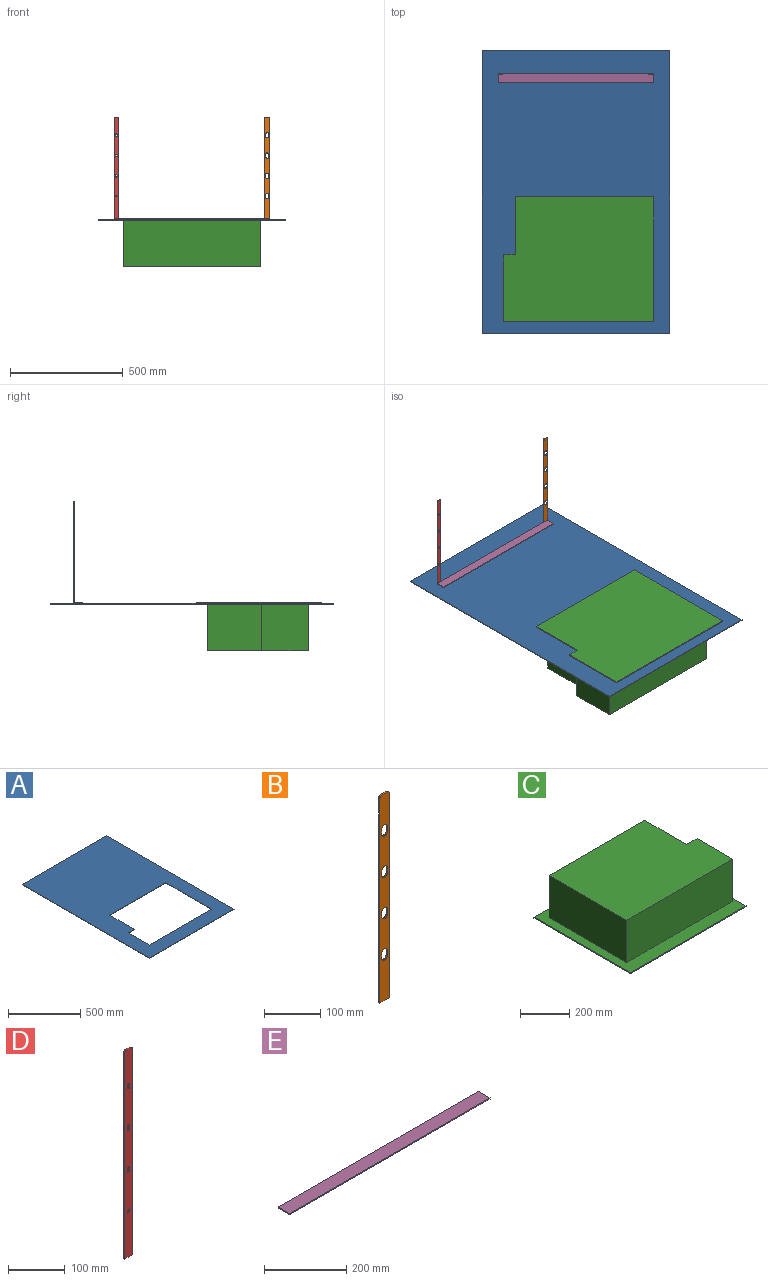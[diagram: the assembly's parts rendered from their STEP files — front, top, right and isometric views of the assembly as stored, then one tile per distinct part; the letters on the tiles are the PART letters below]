
ASSEMBLY  parts=5 mates=4
PART A: 12 faces, bbox 831x1250x3 mm
  f0: plane 831x3mm, normal (0,1,0), area 2493mm2, adj f1,f9,f10,f11
  f1: plane 1250x3mm, normal (-1,0,0), area 3750mm2, adj f0,f2,f10,f11
  f2: plane 831x3mm, normal (0,-1,0), area 2493mm2, adj f1,f9,f10,f11
  f3: plane 551x3mm, normal (0,-1,0), area 1653mm2, adj f4,f8,f10,f11
  f4: plane 448.19x3mm, normal (-1,0,0), area 1344.6mm2, adj f3,f5,f10,f11
  f5: plane 611x3mm, normal (0,1,0), area 1833mm2, adj f4,f6,f10,f11
  f6: plane 206.5x3mm, normal (1,0,0), area 619.5mm2, adj f5,f7,f10,f11
  f7: plane 60x3mm, normal (0,-1,0), area 180mm2, adj f6,f8,f10,f11
  f8: plane 241.69x3mm, normal (1,0,0), area 725.1mm2, adj f3,f7,f10,f11
  f9: plane 1250x3mm, normal (1,0,0), area 3750mm2, adj f0,f2,f10,f11
  f10: plane 1250x831mm, normal (0,0,1), area 779410.1mm2, adj f0,f1,f2,f3,f4,f5,f6,f7
  f11: plane 1250x831mm, normal (0,0,-1), area 779410.1mm2, adj f0,f1,f2,f3,f4,f5,f6,f7
PART B: 24 faces, bbox 24.2x3x450 mm
  f0: plane 10x3mm, normal (1,0,0), area 30mm2, adj f1,f21,f22,f23
  f1: cylinder r=7.1mm len=14.2mm, axis (0,-1,0), area 66.9mm2, adj f0,f2,f22,f23
  f2: plane 10x3mm, normal (-1,0,0), area 30mm2, adj f1,f21,f22,f23
  f3: plane 10x3mm, normal (1,0,0), area 30mm2, adj f4,f17,f22,f23
  f4: cylinder r=7.1mm len=14.2mm, axis (0,-1,0), area 66.9mm2, adj f3,f5,f22,f23
  f5: plane 10x3mm, normal (-1,0,0), area 30mm2, adj f4,f17,f22,f23
  f6: plane 10x3mm, normal (1,0,0), area 30mm2, adj f7,f18,f22,f23
  f7: cylinder r=7.1mm len=14.2mm, axis (0,-1,0), area 66.9mm2, adj f6,f8,f22,f23
  f8: plane 10x3mm, normal (-1,0,0), area 30mm2, adj f7,f18,f22,f23
  f9: plane 10x3mm, normal (1,0,0), area 30mm2, adj f10,f19,f22,f23
  f10: cylinder r=7.1mm len=14.2mm, axis (0,-1,0), area 66.9mm2, adj f9,f11,f22,f23
  f11: plane 10x3mm, normal (-1,0,0), area 30mm2, adj f10,f19,f22,f23
  f12: plane 445x3mm, normal (-1,0,0), area 1335mm2, adj f13,f20,f22,f23
  f13: plane 24.2x3mm, normal (0,0,-1), area 72.6mm2, adj f12,f14,f22,f23
  f14: plane 445x3mm, normal (1,0,0), area 1335mm2, adj f13,f15,f22,f23
  f15: cylinder r=5mm len=5mm, axis (0,-1,0), area 23.6mm2, adj f14,f16,f22,f23
  f16: plane 14.2x3mm, normal (0,0,1), area 42.6mm2, adj f15,f20,f22,f23
  f17: cylinder r=7.1mm len=14.2mm, axis (0,-1,0), area 66.9mm2, adj f3,f5,f22,f23
  f18: cylinder r=7.1mm len=14.2mm, axis (0,-1,0), area 66.9mm2, adj f6,f8,f22,f23
  f19: cylinder r=7.1mm len=14.2mm, axis (0,-1,0), area 66.9mm2, adj f9,f11,f22,f23
  f20: cylinder r=5mm len=5mm, axis (0,-1,0), area 23.6mm2, adj f12,f16,f22,f23
  f21: cylinder r=7.1mm len=14.2mm, axis (0,-1,0), area 66.9mm2, adj f0,f2,f22,f23
  f22: plane 450x24.2mm, normal (0,1,0), area 9677.8mm2, adj f0,f1,f2,f3,f4,f5,f6,f7
  f23: plane 450x24.2mm, normal (0,-1,0), area 9677.8mm2, adj f0,f1,f2,f3,f4,f5,f6,f7
PART C: 15 faces, bbox 665x553.5x215 mm
  f0: plane 553.5x5mm, normal (-1,0,0), area 2767.5mm2, adj f1,f5,f6,f7
  f1: plane 665x5mm, normal (0,-1,0), area 3325mm2, adj f0,f2,f6,f7
  f2: plane 296x5mm, normal (1,0,0), area 1480mm2, adj f1,f3,f6,f7
  f3: plane 50x5mm, normal (0,1,0), area 250mm2, adj f2,f4,f6,f7
  f4: plane 257.5x5mm, normal (1,0,0), area 1287.5mm2, adj f3,f5,f6,f7
  f5: plane 615x5mm, normal (0,1,0), area 3075mm2, adj f0,f4,f6,f7
  f6: plane 665x553.5mm, normal (0,0,1), area 96890.8mm2, adj f0,f1,f2,f3,f4,f5,f9,f10
  f7: plane 665x553.5mm, normal (0,0,-1), area 355202.5mm2, adj f0,f1,f2,f3,f4,f5
  f8: plane 610x447.19mm, normal (0,0,1), area 258311.7mm2, adj f9,f10,f11,f12,f13,f14
  f9: plane 241.19x210mm, normal (1,0,0), area 50648.8mm2, adj f6,f8,f10,f14
  f10: plane 210x60mm, normal (0,1,0), area 12600mm2, adj f6,f8,f9,f11
  f11: plane 210x206mm, normal (1,0,0), area 43260mm2, adj f6,f8,f10,f12
  f12: plane 610x210mm, normal (0,-1,0), area 128100mm2, adj f6,f8,f11,f13
  f13: plane 447.19x210mm, normal (-1,0,0), area 93908.8mm2, adj f6,f8,f12,f14
  f14: plane 550x210mm, normal (0,1,0), area 115500mm2, adj f6,f8,f9,f13
PART D: 21 faces, bbox 20x3x450 mm
  f0: plane 5x3mm, normal (-1,0,0), area 15mm2, adj f1,f14,f19,f20
  f1: cylinder r=3.5mm len=7mm, axis (0,-1,0), area 33mm2, adj f0,f2,f19,f20
  f2: plane 5x3mm, normal (1,0,0), area 15mm2, adj f1,f14,f19,f20
  f3: plane 5x3mm, normal (-1,0,0), area 15mm2, adj f4,f15,f19,f20
  f4: cylinder r=3.5mm len=7mm, axis (0,-1,0), area 33mm2, adj f3,f5,f19,f20
  f5: plane 5x3mm, normal (1,0,0), area 15mm2, adj f4,f15,f19,f20
  f6: plane 5x3mm, normal (-1,0,0), area 15mm2, adj f7,f16,f19,f20
  f7: cylinder r=3.5mm len=7mm, axis (0,-1,0), area 33mm2, adj f6,f8,f19,f20
  f8: plane 5x3mm, normal (1,0,0), area 15mm2, adj f7,f16,f19,f20
  f9: plane 20x3mm, normal (0,0,-1), area 60mm2, adj f10,f17,f19,f20
  f10: plane 445x3mm, normal (1,0,0), area 1335mm2, adj f9,f11,f19,f20
  f11: cylinder r=5mm len=5mm, axis (0,-1,0), area 23.6mm2, adj f10,f12,f19,f20
  f12: plane 10x3mm, normal (0,0,1), area 30mm2, adj f11,f13,f19,f20
  f13: cylinder r=5mm len=5mm, axis (0,-1,0), area 23.6mm2, adj f12,f17,f19,f20
  f14: cylinder r=3.5mm len=7mm, axis (0,-1,0), area 33mm2, adj f0,f2,f19,f20
  f15: cylinder r=3.5mm len=7mm, axis (0,-1,0), area 33mm2, adj f3,f5,f19,f20
  f16: cylinder r=3.5mm len=7mm, axis (0,-1,0), area 33mm2, adj f6,f8,f19,f20
  f17: plane 445x3mm, normal (-1,0,0), area 1335mm2, adj f9,f13,f19,f20
  f18: cylinder r=3.15mm len=6.3mm, axis (0,-1,0), area 59.4mm2, adj f19,f20
  f19: plane 450x20mm, normal (0,1,0), area 8737.6mm2, adj f0,f1,f2,f3,f4,f5,f6,f7
  f20: plane 450x20mm, normal (0,-1,0), area 8737.6mm2, adj f0,f1,f2,f3,f4,f5,f6,f7
PART E: 6 faces, bbox 691.1x40x3 mm
  f0: plane 691.1x40mm, normal (0,0,1), area 27644mm2, adj f1,f3,f4,f5
  f1: plane 40x3mm, normal (-1,0,0), area 120mm2, adj f0,f2,f4,f5
  f2: plane 691.1x40mm, normal (0,0,-1), area 27644mm2, adj f1,f3,f4,f5
  f3: plane 40x3mm, normal (1,0,0), area 120mm2, adj f0,f2,f4,f5
  f4: plane 691.1x3mm, normal (0,1,0), area 2073.3mm2, adj f0,f1,f2,f3
  f5: plane 691.1x3mm, normal (0,-1,0), area 2073.3mm2, adj f0,f1,f2,f3
PLACE A rot(axis=(-1,0,0),0deg) t=(756,-738.17,-170.42)mm
PLACE B rot(axis=(0,0,1),180deg) t=(901.21,-186.38,-28.61)mm
PLACE C rot(axis=(0,-1,0),180deg) t=(692.83,-957.54,-162.42)mm
PLACE D rot(axis=(0,0,1),180deg) t=(901.21,-186.38,-28.61)mm
PLACE E rot(axis=(0,0,1),180deg) t=(901.21,-186.38,-28.61)mm
MATE fastened E.f0 <-> D.f9  axis (0,0,1) through (348.54,-186.38,-164.42)mm
MATE fastened A.f10 <-> C.f6  axis (0,0,1) through (694.09,-1226.38,-167.42)mm
MATE fastened E.f0 <-> B.f13  axis (0,0,1) through (1039.64,-186.38,-164.42)mm
MATE fastened E.f2 <-> A.f10  axis (0,0,-1) through (694.09,-186.38,-167.42)mm
